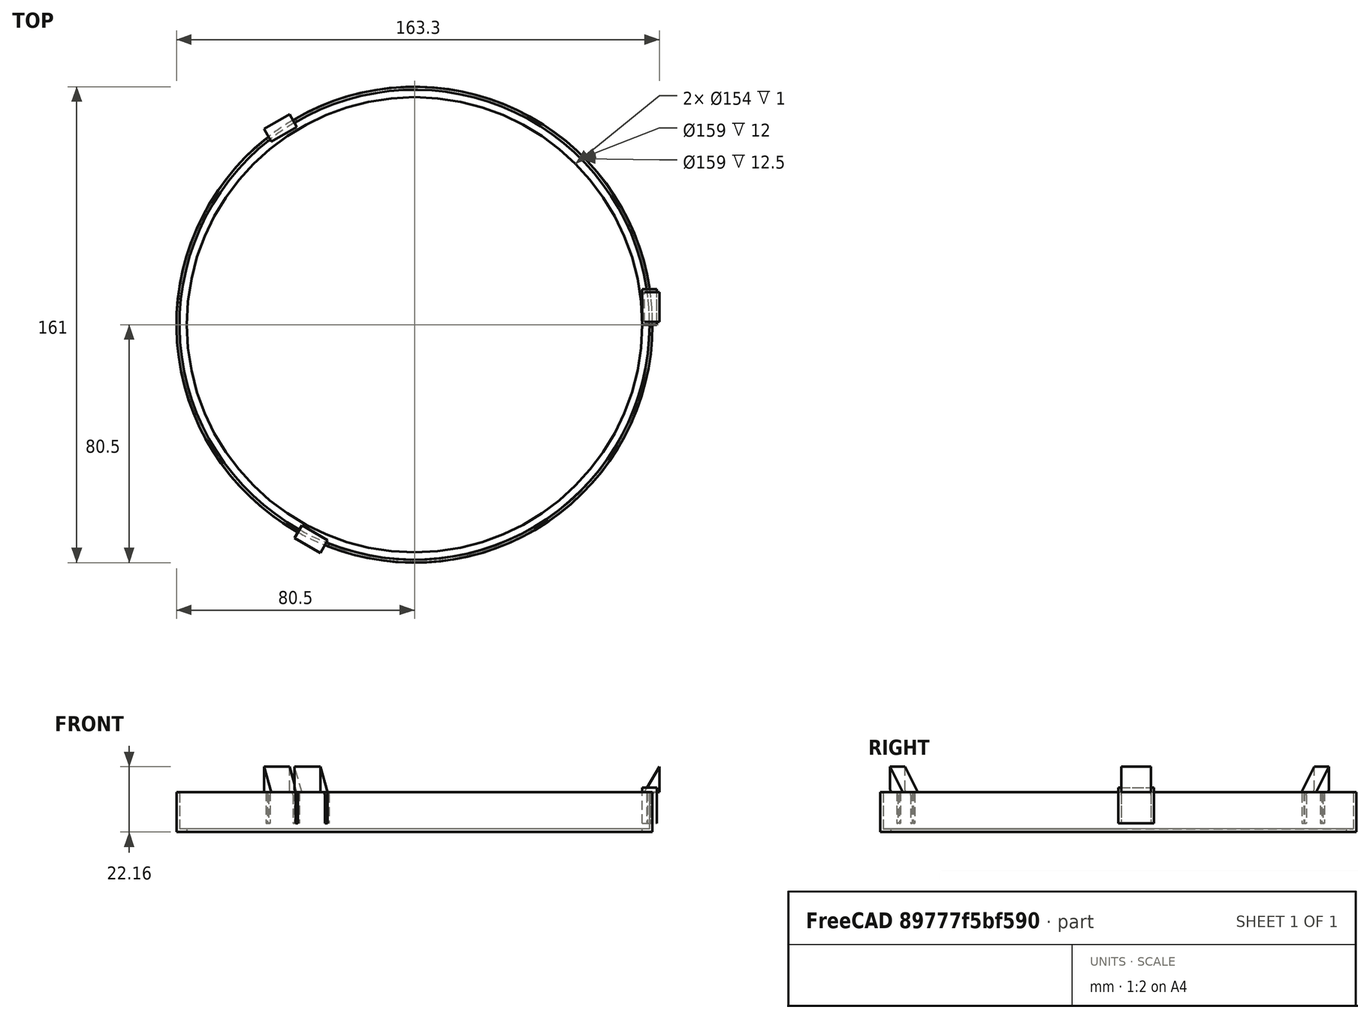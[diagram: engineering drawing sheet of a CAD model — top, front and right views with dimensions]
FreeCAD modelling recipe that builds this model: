
FCSTD DOCUMENT  (FreeCAD 1.0R1.0.0)
Label: Monoblock Pipe Hose Clip
License: All rights reserved
LicenseURL: http://en.wikipedia.org/wiki/All_rights_reserved
objects: Part::Cylinder×8, Part::MultiFuse×4, Part::Cut×4, Part::Box×4, Part::FeaturePython×2, Part::MultiCommon×2, Part::Fillet×2, Spreadsheet::Sheet×1
note: 24 computed .brp shape members not serialized (recipe doc carries the construction recipe); baked Part::Feature solids carry a one-line shape summary decoded from their .brp

FEATURE [Spreadsheet::Sheet] Spreadsheet  label="ACHoseAdapter"
  cells = A1='Model setting; E1='Calculated properties; A2='Hose OD; B2(hose_od)=158; C2='Outer diameter of the hose; E2='Flow cross section; F2(crosssect_flow)==hose_id / 2 * pi; G2='The cross section for airflow. In optimal case keep constant; A3='Hose ID; B3(hose_id)=120; C3='Used for cross section calculations (Note: Estimated at the moment); A4='Hose clamp depth; B4(clamp_depth)=12; C4='Depth of clamping space; A5='Counter diameter; B5(clamp_counterareainset)=2; C5='Area on which the hose is pushed against; A6='Clamp inset; B6(clamp_inset)=1.2; C6='Distance the clamps go inwards into the hose section; A7='Adjustable settings; A8='Tolerance; B8(tolerance)=0.5; C8='Add this tolerance to all spacings; A9='Attachment Thickness; B9(addendum)=1; C9='This is the area the model extends to the bottom to attach to other models; A10='Wall thickness; B10(wallthickness)=1; C10='Thickness of the PLA walls
FEATURE [Part::Cylinder] Cylinder
  Angle = 360
  AttacherType = Attacher::AttachEngine3D
  FirstAngle = 0
  Height = 1
  Radius = 77
  SecondAngle = 0
  expr: Height = <<ACHoseAdapter>>.addendum
  expr: Radius = <<ACHoseAdapter>>.hose_od / 2 - <<ACHoseAdapter>>.clamp_counterareainset
FEATURE [Part::Cylinder] Cylinder001
  Angle = 360
  AttacherType = Attacher::AttachEngine3D
  FirstAngle = 0
  Height = 12.5
  Placement = pos=(0,0,1) rot=(0,0,1;0rad)
  Radius = 79.5
  SecondAngle = 0
  expr: .Placement.Base.z = <<ACHoseAdapter>>.addendum
  expr: Height = <<ACHoseAdapter>>.clamp_depth + <<ACHoseAdapter>>.tolerance
  expr: Radius = <<ACHoseAdapter>>.hose_od / 2 + <<ACHoseAdapter>>.tolerance
FEATURE [Part::Cylinder] Cylinder002
  Angle = 360
  AttacherType = Attacher::AttachEngine3D
  FirstAngle = 0
  Height = 13.5
  Radius = 80.5
  SecondAngle = 0
  expr: Height = <<ACHoseAdapter>>.clamp_depth + <<ACHoseAdapter>>.tolerance + <<ACHoseAdapter>>.addendum
  expr: Radius = <<ACHoseAdapter>>.hose_od / 2 + <<ACHoseAdapter>>.tolerance + <<ACHoseAdapter>>.wallthickness
FEATURE [Part::MultiFuse] Fusion
  Shapes = -> [Cylinder001,Cylinder]
FEATURE [Part::Cut] Cut  label="AttachmentSeatRecess_NoClamps"
  Base = -> Cylinder002
  Tool = -> Fusion
FEATURE [Part::Box] Box  label="Cube"
  AttacherType = Attacher::AttachEngine3D
  Height = 12
  Length = 5
  Placement = pos=(77,0,3) rot=(0,0,1;0rad)
  Width = 12
  expr: .Placement.Base.x = <<ACHoseAdapter>>.hose_od / 2 - 2
  expr: .Placement.Base.z = <<ACHoseAdapter>>.addendum + 2
  expr: Height = <<ACHoseAdapter>>.clamp_depth
  expr: Width = 10 + 2
FEATURE [Part::FeaturePython] Array  # Draft array (typed FeaturePython)
  AlwaysSyncPlacement = false
  Angle = 360
  ArrayType = 1
  Axis = (0,0,1)
  Base = -> Box
  Center = (0,0,0)
  Count = 3
  ExpandArray = false
  Fuse = false
  IntervalAxis = (0,0,0)
  IntervalX = (50,0,0)
  IntervalY = (0,50,0)
  IntervalZ = (0,0,50)
  NumberCircles = 3
  NumberPolar = 3
  NumberX = 2
  NumberY = 2
  NumberZ = 1
  PlacementList = 3 placements: [(77,0,3),(-38.5,66.684,3),(-38.5,-66.684,3)]
  RadialDistance = 50
  ScaleList = (3) [(1,1,1),(1,1,1),(1,1,1)]
  Symmetry = 1
  TangentialDistance = 25
FEATURE [Part::Box] Box001  label="Cube001"
  AttacherType = Attacher::AttachEngine3D
  Height = 12
  Length = 5
  Placement = pos=(77.8,1,3) rot=(0,0,1;0rad)
  Width = 10
  expr: .Placement.Base.x = <<ACHoseAdapter>>.hose_od / 2 - <<ACHoseAdapter>>.clamp_inset
  expr: .Placement.Base.z = <<ACHoseAdapter>>.addendum + 2
  expr: Height = <<ACHoseAdapter>>.clamp_depth
  expr: Width = 10
FEATURE [Part::Cylinder] Cylinder003
  Angle = 360
  AttacherType = Attacher::AttachEngine3D
  FirstAngle = 0
  Height = 13.5
  Radius = 79.5
  SecondAngle = 0
  expr: .Placement.Base.z = 0
  expr: Height = <<ACHoseAdapter>>.clamp_depth + <<ACHoseAdapter>>.tolerance + <<ACHoseAdapter>>.addendum
  expr: Radius = <<ACHoseAdapter>>.hose_od / 2 + <<ACHoseAdapter>>.tolerance
FEATURE [Part::Cylinder] Cylinder004
  Angle = 360
  AttacherType = Attacher::AttachEngine3D
  FirstAngle = 0
  Height = 13.5
  Radius = 80.5
  SecondAngle = 0
  expr: Height = <<ACHoseAdapter>>.clamp_depth + <<ACHoseAdapter>>.tolerance + <<ACHoseAdapter>>.addendum
  expr: Radius = <<ACHoseAdapter>>.hose_od / 2 + <<ACHoseAdapter>>.tolerance + <<ACHoseAdapter>>.wallthickness
FEATURE [Part::Cut] Cut001
  Base = -> Cylinder004
  Tool = -> Cylinder003
FEATURE [Part::MultiCommon] Common
  Shapes = -> [Box001,Cut001]
FEATURE [Part::Box] Box002  label="Cube002"
  AttacherType = Attacher::AttachEngine3D
  Height = 12
  Length = 5
  Placement = pos=(77.8,1,13.5) rot=(0,0,1;0rad)
  Width = 10
  expr: .Placement.Base.x = <<ACHoseAdapter>>.hose_od / 2 - <<ACHoseAdapter>>.clamp_inset
  expr: .Placement.Base.z = <<ACHoseAdapter>>.addendum + <<ACHoseAdapter>>.clamp_depth + <<ACHoseAdapter>>.tolerance
  expr: Height = <<ACHoseAdapter>>.clamp_depth
  expr: Width = 10
FEATURE [Part::Box] Box003  label="Cube003"
  AttacherType = Attacher::AttachEngine3D
  Height = 12
  Length = 5
  Placement = pos=(77.8,1,13.5) rot=(0,1,0;0.523599rad)
  Width = 10
  expr: .Placement.Base.x = <<ACHoseAdapter>>.hose_od / 2 - <<ACHoseAdapter>>.clamp_inset
  expr: .Placement.Base.z = <<ACHoseAdapter>>.addendum + <<ACHoseAdapter>>.clamp_depth + <<ACHoseAdapter>>.tolerance
  expr: Height = <<ACHoseAdapter>>.clamp_depth
  expr: Width = 10
FEATURE [Part::MultiCommon] Common001
  Shapes = -> [Box003,Box002]
FEATURE [Part::MultiFuse] Fusion001  label="ClampSingle"
  Shapes = -> [Common,Common001]
FEATURE [Part::FeaturePython] Array001  # Draft array (typed FeaturePython)
  AlwaysSyncPlacement = false
  Angle = 360
  ArrayType = 1
  Axis = (0,0,1)
  Base = -> Fusion001
  Center = (0,0,0)
  Count = 3
  ExpandArray = false
  Fuse = false
  IntervalAxis = (0,0,0)
  IntervalX = (50,0,0)
  IntervalY = (0,50,0)
  IntervalZ = (0,0,50)
  NumberCircles = 3
  NumberPolar = 3
  NumberX = 2
  NumberY = 2
  NumberZ = 1
  PlacementList = 3 placements: [(0,0,0),(0,0,0),(0,0,0)]
  RadialDistance = 50
  ScaleList = (3) [(1,1,1),(1,1,1),(1,1,1)]
  Symmetry = 1
  TangentialDistance = 25
FEATURE [Part::Cylinder] Cylinder005
  Angle = 360
  AttacherType = Attacher::AttachEngine3D
  FirstAngle = 0
  Height = 1
  Radius = 77
  SecondAngle = 0
  expr: Height = <<ACHoseAdapter>>.addendum
  expr: Radius = <<ACHoseAdapter>>.hose_od / 2 - <<ACHoseAdapter>>.clamp_counterareainset
FEATURE [Part::Cylinder] Cylinder006
  Angle = 360
  AttacherType = Attacher::AttachEngine3D
  FirstAngle = 0
  Height = 12.5
  Placement = pos=(0,0,1) rot=(0,0,1;0rad)
  Radius = 79.5
  SecondAngle = 0
  expr: .Placement.Base.z = <<ACHoseAdapter>>.addendum
  expr: Height = <<ACHoseAdapter>>.clamp_depth + <<ACHoseAdapter>>.tolerance
  expr: Radius = <<ACHoseAdapter>>.hose_od / 2 + <<ACHoseAdapter>>.tolerance
FEATURE [Part::Cylinder] Cylinder007
  Angle = 360
  AttacherType = Attacher::AttachEngine3D
  FirstAngle = 0
  Height = 13.5
  Radius = 80.5
  SecondAngle = 0
  expr: Height = <<ACHoseAdapter>>.clamp_depth + <<ACHoseAdapter>>.tolerance + <<ACHoseAdapter>>.addendum
  expr: Radius = <<ACHoseAdapter>>.hose_od / 2 + <<ACHoseAdapter>>.tolerance + <<ACHoseAdapter>>.wallthickness
FEATURE [Part::MultiFuse] Fusion002
  Shapes = -> [Cylinder006,Cylinder005]
FEATURE [Part::Cut] Cut002  label="AttachmentSeatRecess_NoClamps001"
  Base = -> Cylinder007
  Tool = -> Fusion002
FEATURE [Part::Cut] Cut003
  Base = -> Cut002
  Tool = -> Array
FEATURE [Part::MultiFuse] Fusion003
  Shapes = -> [Cut003,Array001]
FEATURE [Part::Fillet] Fillet
  Base = -> Fusion003
  EdgeLinks = -> Fusion003 [Edge25,Edge39,Edge53]
  Edges = 3 edges r=0.5: [Edge25,Edge39,Edge53]
FEATURE [Part::Fillet] Fillet001
  Base = -> Fillet
  EdgeLinks = -> Fillet [Edge52,Edge64,Edge76,Edge92,Edge97,Edge101]
  Edges = 6 edges r=1: [Edge52,Edge64,Edge76,Edge92,Edge97,Edge101]
